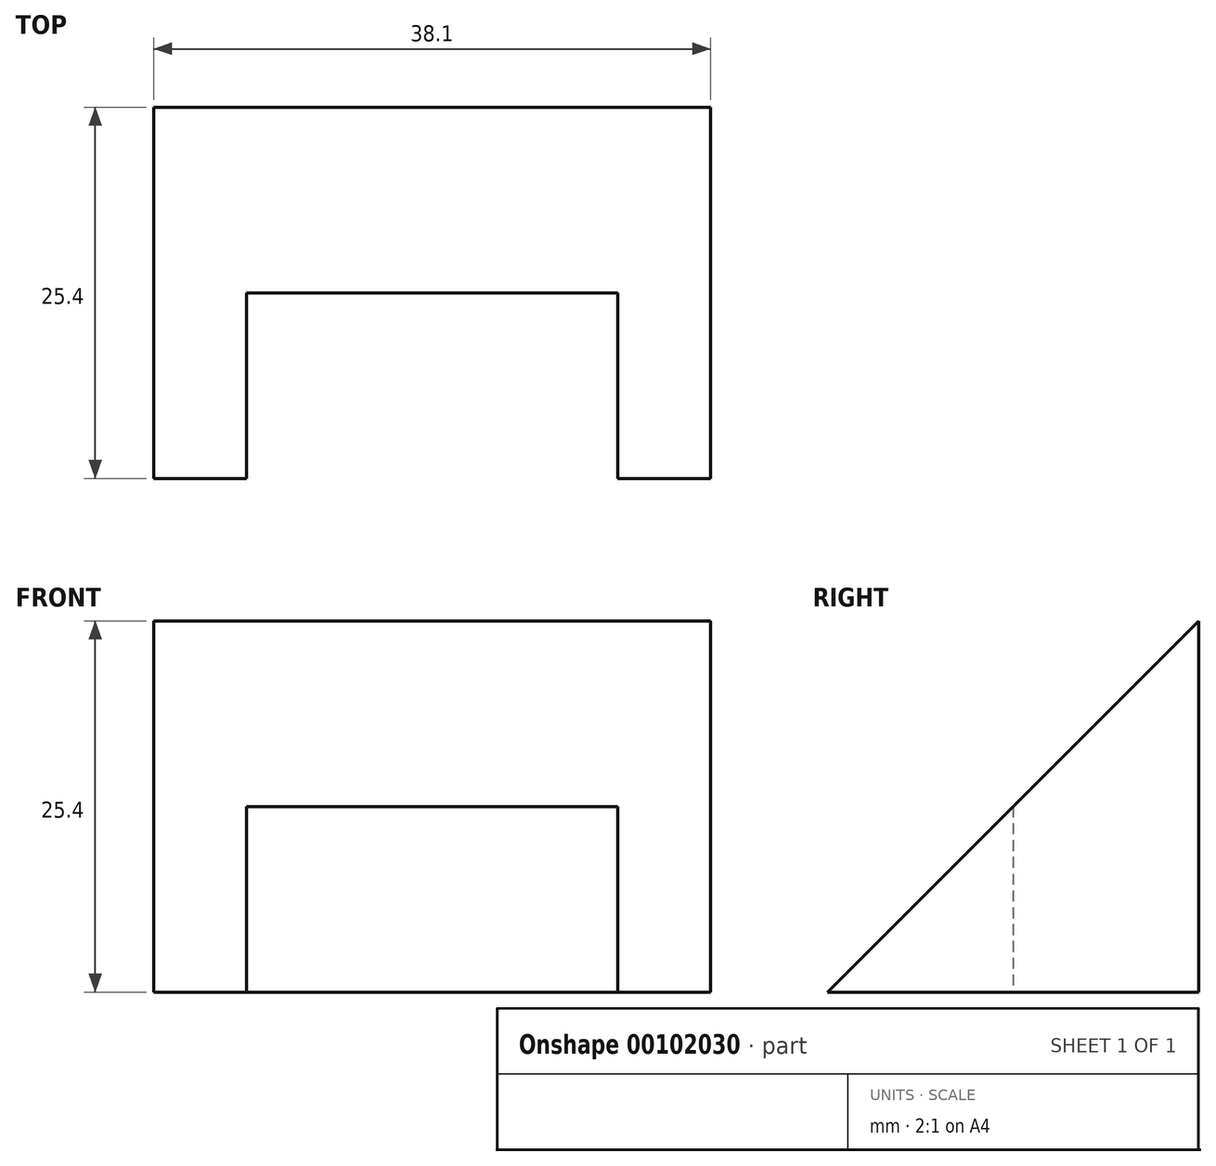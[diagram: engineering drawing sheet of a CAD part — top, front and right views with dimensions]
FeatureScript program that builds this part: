
annotation { "Feature Type Name" : "Feature", "Feature Type Description" : "" }
export const myFeature = defineFeature(function(context is Context, id is Id, definition is map)
    precondition{}
    {
        {
            var Q0;
            Q0=qCreatedBy(makeId("Right.planeOp"),FACE);
            var sketch = newSketch(context, id + "F0", { "sketchPlane" : qUnion([Q0])});
            skLineSegment(sketch, "E0", {"start": v(0, 0) * mm, "end": v(25.4, 0) * mm});
            skLineSegment(sketch, "E1", {"start": v(25.4, 0) * mm, "end": v(25.4, 25.4) * mm});
            skLineSegment(sketch, "E2", {"start": v(25.4, 25.4) * mm, "end": v(0, 25.4) * mm});
            skLineSegment(sketch, "E3", {"start": v(0, 25.4) * mm, "end": v(0, 0) * mm});
            skSolve(sketch);
        }
        {
            var Q0;
            Q0 = qSketchRegion(id + "F0", true);
            extrude(context, id + "F1", {"entities" : qUnion([Q0]), "oppositeDirection" : true, "depth" : 38.1 * mm});
        }
        {
            var Q0;
            Q0=qCreatedBy(makeId("Right.planeOp"),FACE);
            var sketch = newSketch(context, id + "F2", { "sketchPlane" : qUnion([Q0])});
            skLineSegment(sketch, "E4", {"start": v(0, 0) * mm, "end": v(0, 25.4) * mm});
            skLineSegment(sketch, "E5", {"start": v(0, 25.4) * mm, "end": v(25.4, 25.4) * mm});
            skLineSegment(sketch, "E6", {"start": v(25.4, 25.4) * mm, "end": v(0, 0) * mm});
            skSolve(sketch);
        }
        {
            var Q0;
            Q0 = qSketchRegion(id + "F2", true);
            extrude(context, id + "F3", {"entities" : qUnion([Q0]), "operationType" : NewBodyOperationType.REMOVE, "oppositeDirection" : true, "depth" : 38.1 * mm});
        }
        {
            var Q0;
            Q0=qCreatedBy(makeId("Right.planeOp"),FACE);
            var sketch = newSketch(context, id + "F4", { "sketchPlane" : qUnion([Q0])});
            skLineSegment(sketch, "E7", {"start": v(0, 0) * mm, "end": v(12.7, 12.7) * mm});
            skLineSegment(sketch, "E8", {"start": v(12.7, 12.7) * mm, "end": v(12.7, 0) * mm});
            skLineSegment(sketch, "E9", {"start": v(12.7, 0) * mm, "end": v(0, 0) * mm});
            skSolve(sketch);
        }
        {
            var Q0;
            Q0 = qSketchRegion(id + "F4", true);
            extrude(context, id + "F5", {"entities" : qUnion([Q0]), "operationType" : NewBodyOperationType.REMOVE, "oppositeDirection" : true, "depth" : 31.75 * mm, "hasSecondDirection" : true, "secondDirectionOppositeDirection" : true, "secondDirectionDepth" : 6.35 * mm});
        }
    });
